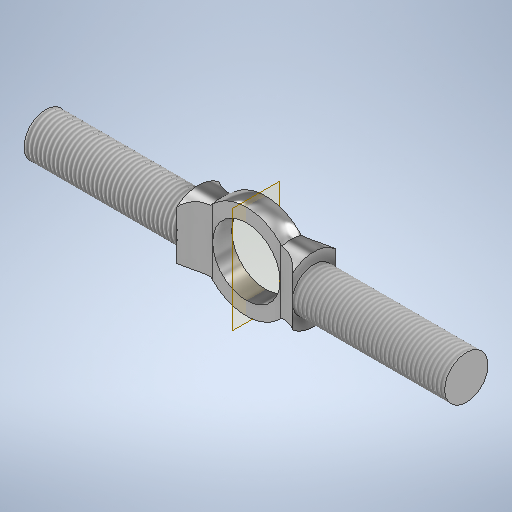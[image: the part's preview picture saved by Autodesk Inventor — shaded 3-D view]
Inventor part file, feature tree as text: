
AUTODESK INVENTOR PART (.ipt)
format: ipt  version: 2025.2 (Build 292293000, 293)  size: 342,016 bytes
history: native  units: in
note: dims shown in document units (in); Inventor stores cm internally (conversion verified against a paired STEP export)
features: other x3, extrude x2, thread x2, revolve x1, plane x1
ambient origin geometry x8: Origin, YZ Plane, XZ Plane, XY Plane, X Axis, Y Axis, Z Axis, Center Point
bodies: Volumenkörper1 (feature_tree)
feature tree (9):
  other  "Skelett_Laufkatze.ipt"
  revolve  "Umdrehung1"
  extrude  "Extrusion1"  Depth=0.3937in
  extrude  "Extrusion2"  TaperAngle=90.0deg  [1 undecoded]
  thread  "Gewinde1"  [1 undecoded]
  thread  "Gewinde2"  [1 undecoded]
  plane  "Arbeitsebene2"
  other  "Schraubbolzen_oben"
  other  "Schraubbolzen_Ankerausschnitt"
note: 3 required parameter values undecoded (feature->parameter linkage not recoverable at this tier; creation-order binding heuristic only, values carry confidence <= 0.55)
